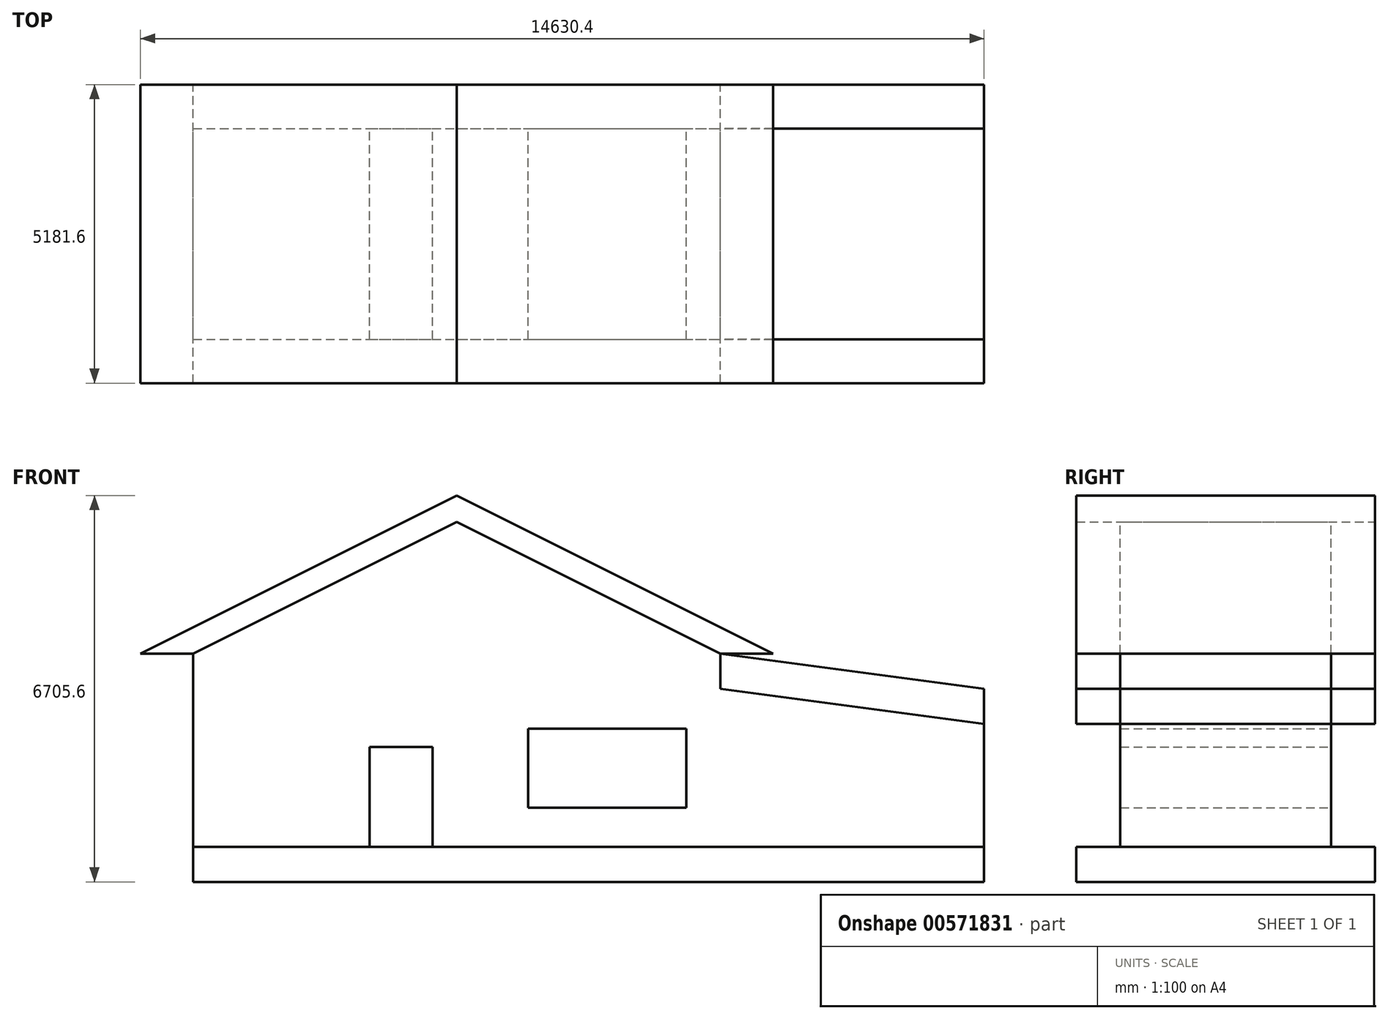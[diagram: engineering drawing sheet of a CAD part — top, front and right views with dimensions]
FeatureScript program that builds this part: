
annotation { "Feature Type Name" : "Feature", "Feature Type Description" : "" }
export const myFeature = defineFeature(function(context is Context, id is Id, definition is map)
    precondition{}
    {
        {
            var Q0;
            Q0=qCreatedBy(makeId("Front.planeOp"),FACE);
            var sketch = newSketch(context, id + "F0", { "sketchPlane" : qUnion([Q0])});
            skLineSegment(sketch, "E0", {"start": v(0, 0) * mm, "end": v(-4572, 0) * mm});
            skLineSegment(sketch, "E1", {"start": v(0, 0) * mm, "end": v(4572, 0) * mm});
            skLineSegment(sketch, "E2", {"start": v(0, 0) * mm, "end": v(0, 2286) * mm});
            skLineSegment(sketch, "E3", {"start": v(0, 2286) * mm, "end": v(4572, 0) * mm});
            skLineSegment(sketch, "E4", {"start": v(-4572, 0) * mm, "end": v(0, 2286) * mm});
            skLineSegment(sketch, "E5", {"start": v(-4572, 0) * mm, "end": v(-5486.4, 0) * mm});
            skLineSegment(sketch, "E6", {"start": v(4572, 0) * mm, "end": v(5486.4, 0) * mm});
            skLineSegment(sketch, "E7", {"start": v(0, 2286) * mm, "end": v(0, 2743.2) * mm});
            skLineSegment(sketch, "E8", {"start": v(-5486.4, 0) * mm, "end": v(0, 2743.2) * mm});
            skLineSegment(sketch, "E9", {"start": v(0, 2743.2) * mm, "end": v(5486.4, 0) * mm});
            skLineSegment(sketch, "E10", {"start": v(-4572, 0) * mm, "end": v(-4572, -3352.8) * mm});
            skLineSegment(sketch, "E11", {"start": v(4572, 0) * mm, "end": v(4572, -3352.8) * mm});
            skLineSegment(sketch, "E12", {"start": v(-4572, -3352.8) * mm, "end": v(-4572, -3962.4) * mm});
            skLineSegment(sketch, "E13", {"start": v(4572, -3352.8) * mm, "end": v(4572, -3962.4) * mm});
            skLineSegment(sketch, "E14", {"start": v(4572, -3962.4) * mm, "end": v(-4572, -3962.4) * mm});
            skLineSegment(sketch, "E15", {"start": v(4572, -3352.8) * mm, "end": v(9144, -3352.8) * mm});
            skLineSegment(sketch, "E16", {"start": v(4572, -3962.4) * mm, "end": v(9144, -3962.4) * mm});
            skLineSegment(sketch, "E17", {"start": v(9144, -3352.8) * mm, "end": v(9144, -3962.4) * mm});
            skLineSegment(sketch, "E18", {"start": v(9144, -3352.8) * mm, "end": v(9144, -609.6) * mm});
            skLineSegment(sketch, "E19", {"start": v(9144, -609.6) * mm, "end": v(4572, 0) * mm});
            skLineSegment(sketch, "E20", {"start": v(4572, 0) * mm, "end": v(4572, -609.6) * mm});
            skLineSegment(sketch, "E21", {"start": v(9144, -609.6) * mm, "end": v(9144, -1219.2) * mm});
            skLineSegment(sketch, "E22", {"start": v(4572, -609.6) * mm, "end": v(9144, -1219.2) * mm});
            skLineSegment(sketch, "E23", {"start": v(1235.93, -2678.06) * mm, "end": v(1235.93, -1306.46) * mm});
            skLineSegment(sketch, "E24", {"start": v(1235.93, -2678.06) * mm, "end": v(3979.13, -2678.06) * mm});
            skLineSegment(sketch, "E25", {"start": v(3979.13, -2678.06) * mm, "end": v(3979.13, -1306.46) * mm});
            skLineSegment(sketch, "E26", {"start": v(3979.13, -1306.46) * mm, "end": v(1235.93, -1306.46) * mm});
            skLineSegment(sketch, "E27.bottom", {"start": v(-1517.62, -1624.07) * mm, "end": v(-424.1, -1624.07) * mm});
            skLineSegment(sketch, "E27.top", {"start": v(-1517.62, -3352.8) * mm, "end": v(-424.1, -3352.8) * mm});
            skLineSegment(sketch, "E27.left", {"start": v(-1517.62, -1624.07) * mm, "end": v(-1517.62, -3352.8) * mm});
            skLineSegment(sketch, "E27.right", {"start": v(-424.1, -1624.07) * mm, "end": v(-424.1, -3352.8) * mm});
            skLineSegment(sketch, "E28", {"start": v(-4572, -3352.8) * mm, "end": v(4572, -3352.8) * mm});
            skText(sketch, "E29", { "text": "allie", "fontName": "OpenSans-Regular.ttf"});
            const initialGuessF0  = {"E29": [-2.92104, -8.27763, 1, 0, 2.7882]};
            skSetInitialGuess(sketch, initialGuessF0);
            skSolve(sketch);
        }
        {
            var Q0;
            Q0=makeQuery(id+"F0.imprint","IMPRINT",FACE,{"disambiguationData":[TD([[makeQuery(id+"F0.imprint","IMPRINT",EDGE,{"derivedFrom":sQuery(id+"F0.wireOp",EDGE,"E4")}),1.0]])]});
            var Q1;
            Q1=makeQuery(id+"F0.imprint","IMPRINT",FACE,{"disambiguationData":[TD([[makeQuery(id+"F0.imprint","IMPRINT",EDGE,{"derivedFrom":sQuery(id+"F0.wireOp",EDGE,"E3")}),1.0]])]});
            var Q2;
            Q2=makeQuery(id+"F0.imprint","IMPRINT",FACE,{"disambiguationData":[TD([[makeQuery(id+"F0.imprint","IMPRINT",EDGE,{"derivedFrom":sQuery(id+"F0.wireOp",EDGE,"E19")}),1.0]])]});
            var Q3;
            Q3=makeQuery(id+"F0.imprint","IMPRINT",FACE,{"disambiguationData":[TD([[makeQuery(id+"F0.imprint","IMPRINT",EDGE,{"derivedFrom":sQuery(id+"F0.wireOp",EDGE,"E13")}),1.0]])]});
            var Q4;
            {var subQ1=sQuery(id+"F0.wireOp",EDGE,"E12");Q4=makeQuery(id+"F0.imprint","IMPRINT",FACE,{"disambiguationData":[TD([[makeQuery(id+"F0.imprint","IMPRINT",EDGE,{"derivedFrom":subQ1}),1.0]])]});}
            extrude(context, id + "F1", {"entities" : qUnion([Q0, Q1, Q2, Q3, Q4]), "endBound" : BoundingType.SYMMETRIC, "depth" : 5181.6 * mm, "offsetDistance" : 30.48 * mm});
        }
        {
            var Q0;
            Q0=makeQuery(id+"F0.imprint","IMPRINT",FACE,{"disambiguationData":[TD([[makeQuery(id+"F0.imprint","IMPRINT",EDGE,{"derivedFrom":sQuery(id+"F0.wireOp",EDGE,"E0")}),-1.0]])]});
            var Q1;
            Q1=makeQuery(id+"F0.imprint","IMPRINT",FACE,{"disambiguationData":[TD([[makeQuery(id+"F0.imprint","IMPRINT",EDGE,{"derivedFrom":sQuery(id+"F0.wireOp",EDGE,"E1")}),1.0]])]});
            var Q2;
            Q2=makeQuery(id+"F0.imprint","IMPRINT",FACE,{"disambiguationData":[TD([[makeQuery(id+"F0.imprint","IMPRINT",EDGE,{"derivedFrom":sQuery(id+"F0.wireOp",EDGE,"E0")}),1.0]])]});
            var Q3;
            Q3=makeQuery(id+"F0.imprint","IMPRINT",FACE,{"disambiguationData":[TD([[makeQuery(id+"F0.imprint","IMPRINT",EDGE,{"derivedFrom":sQuery(id+"F0.wireOp",EDGE,"E11")}),1.0]])]});
            extrude(context, id + "F2", {"entities" : qUnion([Q0, Q1, Q2, Q3]), "endBound" : BoundingType.SYMMETRIC, "depth" : 3657.6 * mm, "offsetDistance" : 30.48 * mm});
        }
    });
